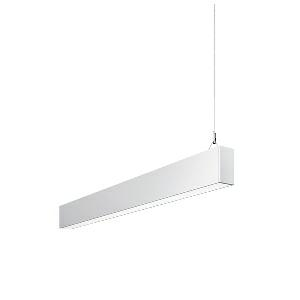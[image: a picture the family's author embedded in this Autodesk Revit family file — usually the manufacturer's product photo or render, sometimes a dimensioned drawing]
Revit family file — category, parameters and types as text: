
# Revit family: dotoo_line_-_dlp_2000_830_d_end_00805808_22fd
name_source: partatom
category: Lighting Fixtures
units: mm (PartAtom-declared; Revit-internal decimal feet)

## family parameters
Cut with Voids When Loaded = No
Host = Face
Light Source = No
Part Type = Normal
Room Calculation Point = No
Round Connector Dimension = Use Diameter
Shared = No

## types (1)
- DOTOO.line - DLP 2000/830/D END (1 x LED, 1650 lm, 3000K)
    Apparent Load = 16 VA
    Approval mark = CE
    CIE Flux Codes = 67 91 98 100 100
    Color Rendering = 80-89
    Color Temperature = 3000K
    Control Gear = Electronic ballast
    Default Elevation = 1800 mm
    Description = DLP 2000/830/D|Suspended luminaire|light source: LED|connected load: 220-240 V, 50/60 Hz|Power consumption: approx. 16 W|standby: approx. 0,15|luminous flux: 1650 lm|luminous efficacy: 103 lm/W|light distribution: Direct|direct ratio: approx. 100 %|colour temperature: Warm white, ca. 3000 K|color rendering index (CRI): >= 80|chromaticity tolerance:  3 SDCM|System of protection: IP 40|technology: Continuously dimmable|luminaire body|material: Sectional aluminium|colour: White|lamp cover: Acrylic (PMMA), Clear|mains lead: 1,0 m With free stranded wires|Fastening: Steel cable 0.3 - 0.7 m|glare control: Prism aperture|luminance(L65): <= 3000 cd/m|unified glare rating(4H 8H): <=  19|special features: DALI Load 1x, TouchDIM - dimming via standard switch, Through-wired, up to 18 m on one mains connection, Flicker-free, Suitable as emergency lighting, Mechanical and electrical connection of the individual modules without tools|
    Frequency = 50 Hz
    Height = 110 mm
    Lamp = 1 x LED
    Lamp Light Flux = 1650 lm
    Lamp count = 1
    Length = 1408 mm
    Luminous efficacy = 103 lm/W
    Manufacturer = Waldmann
    ModVariant = No
    Model = 00805808
    Mounting Place = Ceiling
    Mounting Type = Pendant
    Number of Poles = 1
    OnlyDefault = Yes
    Power Factor = 1
    Product Name = DOTOO.line - DLP 2000/830/D END
    Product group = Suspended luminaire
    ProductGroupID = 9
    Protection Class = Protection class I
    Protection Degree = IP 40
    RLX_Detail_Level = 1
    RLX_Emergency_Light_Flux = 0 lm
    RLX_Emergency_Type = 0
    RLX_Emergency_Type_DB = No
    RlxData = <blob elided: 18349 chars, md5=eb9b0718>
    Socket = socket
    Standby Power = 0 W
    System Light Flux = 1650 lm
    System Power = 16 W
    Type Comments = Product without accessories
    Type Image = 113303000-00692573.jpg
    URL = http://relux.com
    VarID = ---
    Voltage = 230 V
    Voltage Range = 220-240 V
    Weight = 0.00 kg
    Width = 60 mm  [stored 0.19685 ft]

note: [stored X ft] marks values corroborated as IEEE doubles in the binary element streams (Revit-internal decimal feet)

## geometry (parser evidence)
native form markers: Blend x4, Sweep x11
no freeform markers — native parametric forms only
